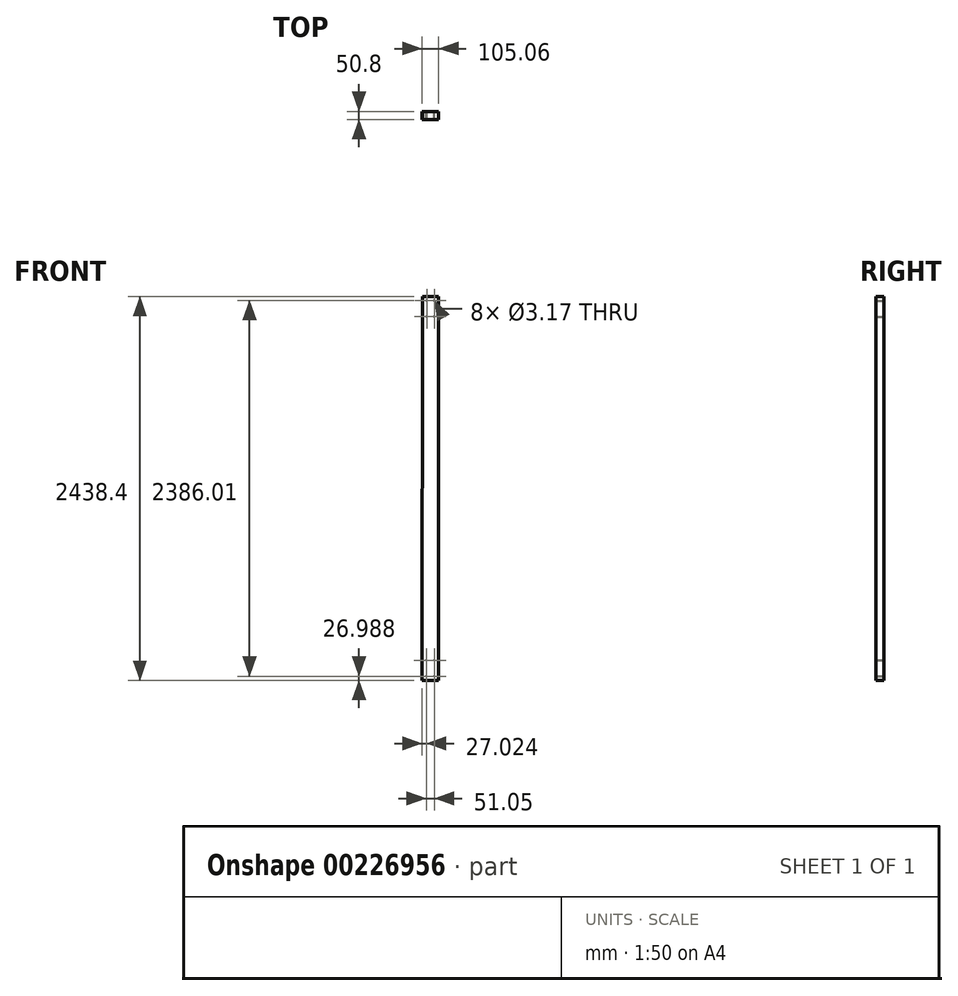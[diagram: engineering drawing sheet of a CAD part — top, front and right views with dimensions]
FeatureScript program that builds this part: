
annotation { "Feature Type Name" : "Feature", "Feature Type Description" : "" }
export const myFeature = defineFeature(function(context is Context, id is Id, definition is map)
    precondition{}
    {
        {
            var Q0;
            Q0=qCreatedBy(makeId("Front.planeOp"),FACE);
            var sketch = newSketch(context, id + "F0", { "sketchPlane" : qUnion([Q0])});
            skLineSegment(sketch, "E0", {"start": v(-55.57, 2438.4) * mm, "end": v(46.03, 2438.4) * mm});
            skLineSegment(sketch, "E1", {"start": v(46.03, 2438.4) * mm, "end": v(46.03, 0) * mm});
            skLineSegment(sketch, "E2", {"start": v(46.03, 0) * mm, "end": v(-59.03, 0) * mm});
            skLineSegment(sketch, "E3", {"start": v(-59.03, 0) * mm, "end": v(-55.57, 2438.4) * mm});
            skCircle(sketch, "E4", {"center": v(-28.62, 2413) * mm, "radius": 1.59 * mm});
            skCircle(sketch, "E5", {"center": v(19.04, 2413) * mm, "radius": 1.59 * mm});
            skCircle(sketch, "E6", {"center": v(-28.76, 2311.4) * mm, "radius": 1.59 * mm});
            skCircle(sketch, "E7", {"center": v(19.04, 2311.4) * mm, "radius": 1.59 * mm});
            skCircle(sketch, "E8", {"center": v(-32, 26.99) * mm, "radius": 1.59 * mm});
            skCircle(sketch, "E9", {"center": v(19.04, 26.99) * mm, "radius": 1.59 * mm});
            skCircle(sketch, "E10", {"center": v(-31.86, 128.59) * mm, "radius": 1.59 * mm});
            skCircle(sketch, "E11", {"center": v(19.04, 128.59) * mm, "radius": 1.59 * mm});
            skSolve(sketch);
        }
        {
            var Q0;
            Q0=makeQuery(id+"F0.imprint","IMPRINT",FACE,{"disambiguationData":[TD([[makeQuery(id+"F0.imprint","IMPRINT",EDGE,{"derivedFrom":sQuery(id+"F0.wireOp",EDGE,"E0")}),-1.0]])]});
            extrude(context, id + "F1", {"entities" : qUnion([Q0]), "depth" : 50.8 * mm});
        }
    });
